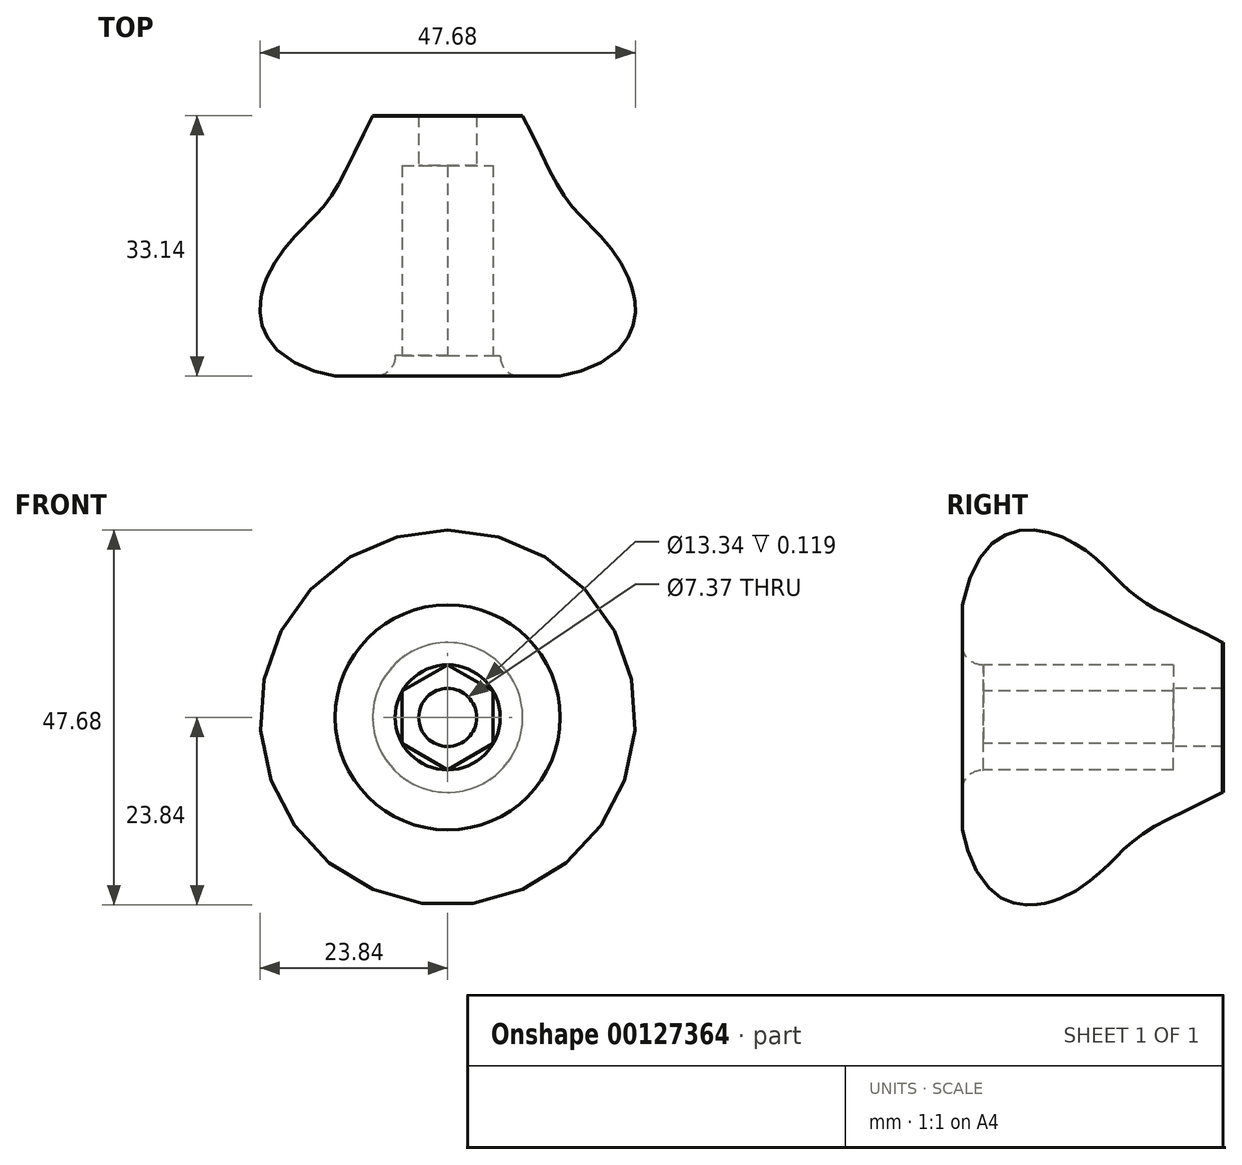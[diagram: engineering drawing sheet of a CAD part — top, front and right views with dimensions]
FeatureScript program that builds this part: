
annotation { "Feature Type Name" : "Feature", "Feature Type Description" : "" }
export const myFeature = defineFeature(function(context is Context, id is Id, definition is map)
    precondition{}
    {
        {
            var Q0;
            Q0=qCreatedBy(makeId("Front.planeOp"),FACE);
            var sketch = newSketch(context, id + "F0", { "sketchPlane" : qUnion([Q0])});
            skCircle(sketch, "E0", {"center": v(0, 0) * mm, "radius": 9.53 * mm});
            skSolve(sketch);
        }
        {
            var Q0;
            {var subQ0=sQuery(id+"F0.wireOp",EDGE,"E0");var subQ1=makeQuery(id+"F0.imprint","INTERSECT",VERTEX,{"derivedFrom":[subQ0,sQuery(id+"F0.wireOp",EDGE,"ea245839-a498-4638-985b-73fae0246c39")]});Q0=makeQuery(id+"F0.imprint","IMPRINT",FACE,{"disambiguationData":[TD([[makeQuery(id+"F0.imprint","IMPRINT",EDGE,{"disambiguationData":[TD([[subQ1,-1.0]])],"derivedFrom":subQ0}),1.0]])]});}
            var Q1;
            Q1=makeQuery(id+"F0.imprint","IMPRINT",FACE,{"disambiguationData":[TD([[makeQuery(id+"F0.imprint","IMPRINT",EDGE,{"derivedFrom":sQuery(id+"F0.wireOp",EDGE,"2dcc8b00-aa93-42b5-8a72-6d1d4eab4258")}),1.0]])]});
            extrude(context, id + "F1", {"entities" : qUnion([Q0, Q1]), "offsetDistance" : 25.4 * mm, "depth" : 15.24 * mm});
        }
        {
            var Q0;
            Q0=makeQuery(id+"F1.opExtrude","CAP_FACE",FACE,{"disambiguationData":[OSD([sQuery(id+"F0.wireOp",EDGE,"E0"),sQuery(id+"F0.wireOp",EDGE,"2dcc8b00-aa93-42b5-8a72-6d1d4eab4258"),sQuery(id+"F0.wireOp",EDGE,"ea245839-a498-4638-985b-73fae0246c39"),sQuery(id+"F0.wireOp",EDGE,"28ef0078-34b0-4df2-9f13-6cd2cfbab48c0.MirrorCS"),sQuery(id+"F0.wireOp",EDGE,"f54b358c-e5d3-4f08-8e52-d21b7307fad60.MirrorCS")])],"isStart":false});
            var sketch = newSketch(context, id + "F2", { "sketchPlane" : qUnion([Q0])});
            skCircle(sketch, "E1.cCircle", {"center": v(0, 0) * mm, "radius": 5.78 * mm, "construction": true});
            skLineSegment(sketch, "E1.0", {"start": v(5.78, 3.34) * mm, "end": v(5.78, -3.34) * mm});
            skLineSegment(sketch, "E1.1", {"start": v(5.78, -3.34) * mm, "end": v(0, -6.67) * mm});
            skLineSegment(sketch, "E1.2", {"start": v(0, -6.67) * mm, "end": v(-5.78, -3.34) * mm});
            skLineSegment(sketch, "E1.3", {"start": v(-5.78, -3.34) * mm, "end": v(-5.78, 3.34) * mm});
            skLineSegment(sketch, "E1.4", {"start": v(-5.78, 3.34) * mm, "end": v(0, 6.67) * mm});
            skLineSegment(sketch, "E1.5", {"start": v(0, 6.67) * mm, "end": v(5.78, 3.34) * mm});
            skPoint(sketch, "E1.0.midPoint", {"position": v(5.78, 0) * mm});
            skSolve(sketch);
        }
        {
            var Q0;
            Q0=makeQuery(id+"F2.imprint","IMPRINT",FACE,{"disambiguationData":[TD([[makeQuery(id+"F2.imprint","IMPRINT",EDGE,{"derivedFrom":sQuery(id+"F2.wireOp",EDGE,"E1.0")}),-1.0]])]});
            extrude(context, id + "F3", {"entities" : qUnion([Q0]), "operationType" : NewBodyOperationType.REMOVE, "oppositeDirection" : true, "depth" : 8.9 * mm});
        }
        {
            var Q0;
            Q0=makeQuery(id+"F3.boolean.opBoolean","COPY",FACE,{"derivedFrom":makeQuery(id+"F3.opExtrude","CAP_FACE",FACE,{"disambiguationData":[OSD([sQuery(id+"F2.wireOp",EDGE,"E1.0"),sQuery(id+"F2.wireOp",EDGE,"E1.1"),sQuery(id+"F2.wireOp",EDGE,"E1.2"),sQuery(id+"F2.wireOp",EDGE,"E1.3"),sQuery(id+"F2.wireOp",EDGE,"E1.4"),sQuery(id+"F2.wireOp",EDGE,"E1.5")])],"isStart":false})});
            var sketch = newSketch(context, id + "F4", { "sketchPlane" : qUnion([Q0])});
            skCircle(sketch, "E2", {"center": v(0, 0) * mm, "radius": 3.68 * mm});
            skSolve(sketch);
        }
        {
            var Q0;
            Q0=makeQuery(id+"F4.imprint","IMPRINT",FACE,{"disambiguationData":[TD([[makeQuery(id+"F4.imprint","IMPRINT",EDGE,{"derivedFrom":sQuery(id+"F4.wireOp",EDGE,"E2")}),1.0]])]});
            extrude(context, id + "F5", {"entities" : qUnion([Q0]), "operationType" : NewBodyOperationType.REMOVE, "endBound" : BoundingType.THROUGH_ALL, "oppositeDirection" : true, "offsetDistance" : 25.4 * mm, "depth" : 25.4 * mm});
        }
        {
            var Q0;
            Q0=qCreatedBy(makeId("Right.planeOp"),FACE);
            var sketch = newSketch(context, id + "F6", { "sketchPlane" : qUnion([Q0])});
            skLineSegment(sketch, "E3", {"start": v(-33.14, -14.3) * mm, "end": v(-33.14, -14.3) * mm});
            skLineSegment(sketch, "E4", {"start": v(-33.14, -14.3) * mm, "end": v(-33.14, 3.71) * mm});
            skLineSegment(sketch, "E5", {"start": v(0, -6.67) * mm, "end": v(-33.14, -6.67) * mm});
            skLineSegment(sketch, "E6", {"start": v(-33.14, 3.71) * mm, "end": v(-33.14, -6.67) * mm});
            skLineSegment(sketch, "E7", {"start": v(0, -6.67) * mm, "end": v(0, -9.47) * mm});
            skFitSpline(sketch, "E8", {"points": [v(0, -9.47) * mm, v(-11.54, -15.77) * mm, v(-19.8, -22.6) * mm, v(-33.14, -14.3) * mm], "startDerivative": vector(-54.08, -28.43) * mm, "endDerivative": vector(-17.97, 89.59) * mm});
            skLineSegment(sketch, "E9", {"start": v(0, 0) * mm, "end": v(-22.32, 0) * mm});
            skSolve(sketch);
        }
        {
            var Q0;
            Q0=makeQuery(id+"F6.imprint","IMPRINT",FACE,{"disambiguationData":[TD([[makeQuery(id+"F6.imprint","IMPRINT",EDGE,{"derivedFrom":sQuery(id+"F6.wireOp",EDGE,"E3")}),-1.0]])]});
            var Q1;
            Q1=makeQuery(id+"F6.imprint","IMPRINT",FACE,{"disambiguationData":[TD([[makeQuery(id+"F6.imprint","IMPRINT",EDGE,{"derivedFrom":sQuery(id+"F6.wireOp",EDGE,"E4")}),-1.0]])]});
            var Q2;
            Q2=sQuery(id+"F6.wireOp",EDGE,"E9");
            revolve(context, id + "F7", {"operationType" : NewBodyOperationType.ADD, "surfaceOperationType" : NewSurfaceOperationType.NEW, "entities" : qUnion([Q0, Q1]), "axis" : qUnion([Q2]), "revolveType" : RevolveType.FULL});
        }
        {
            var Q0;
            Q0=makeQuery(id+"F7.opRevolve","SWEPT_EDGE",EDGE,{"disambiguationData":[OSD([sQuery(id+"F6.wireOp",EDGE,"E5"),sQuery(id+"F6.wireOp",EDGE,"E6")])]});
            fillet(context, id + "F8", {"entities" : qUnion([Q0]), "radius" : 2.54 * mm, "tangentPropagation" : true, "allowEdgeOverflow" : false});
        }
        {
            var Q0;
            {var subQ0=makeQuery(id+"F1.opExtrude","CAP_FACE",FACE,{"disambiguationData":[OSD([sQuery(id+"F0.wireOp",EDGE,"E0")])],"isStart":false});Q0=makeQuery(id+"F7.boolean.opBoolean","SPLIT",FACE,{"disambiguationData":[TD([subQ0,makeQuery(id+"F3.boolean.opBoolean","COPY",FACE,{"derivedFrom":makeQuery(id+"F3.opExtrude","SWEPT_FACE",FACE,{"disambiguationData":[OSD([sQuery(id+"F2.wireOp",EDGE,"E1.3")])]})}),makeQuery(id+"F3.boolean.opBoolean","COPY",FACE,{"derivedFrom":makeQuery(id+"F3.opExtrude","SWEPT_FACE",FACE,{"disambiguationData":[OSD([sQuery(id+"F2.wireOp",EDGE,"E1.4")])]})}),makeQuery(id+"F3.boolean.opBoolean","COPY",FACE,{"derivedFrom":makeQuery(id+"F3.opExtrude","SWEPT_FACE",FACE,{"disambiguationData":[OSD([sQuery(id+"F2.wireOp",EDGE,"E1.5")])]})}),makeQuery(id+"F7.opRevolve","SWEPT_FACE",FACE,{"disambiguationData":[OSD([sQuery(id+"F6.wireOp",EDGE,"E5")])]})])],"derivedFrom":subQ0});}
            var Q1;
            {var subQ0=makeQuery(id+"F1.opExtrude","CAP_FACE",FACE,{"disambiguationData":[OSD([sQuery(id+"F0.wireOp",EDGE,"E0")])],"isStart":false});Q1=makeQuery(id+"F7.boolean.opBoolean","SPLIT",FACE,{"disambiguationData":[TD([subQ0,makeQuery(id+"F3.boolean.opBoolean","COPY",FACE,{"derivedFrom":makeQuery(id+"F3.opExtrude","SWEPT_FACE",FACE,{"disambiguationData":[OSD([sQuery(id+"F2.wireOp",EDGE,"E1.2")])]})}),makeQuery(id+"F3.boolean.opBoolean","COPY",FACE,{"derivedFrom":makeQuery(id+"F3.opExtrude","SWEPT_FACE",FACE,{"disambiguationData":[OSD([sQuery(id+"F2.wireOp",EDGE,"E1.3")])]})}),makeQuery(id+"F3.boolean.opBoolean","COPY",FACE,{"derivedFrom":makeQuery(id+"F3.opExtrude","SWEPT_FACE",FACE,{"disambiguationData":[OSD([sQuery(id+"F2.wireOp",EDGE,"E1.4")])]})}),makeQuery(id+"F7.opRevolve","SWEPT_FACE",FACE,{"disambiguationData":[OSD([sQuery(id+"F6.wireOp",EDGE,"E5")])]})])],"derivedFrom":subQ0});}
            var Q2;
            {var subQ0=makeQuery(id+"F1.opExtrude","CAP_FACE",FACE,{"disambiguationData":[OSD([sQuery(id+"F0.wireOp",EDGE,"E0")])],"isStart":false});Q2=makeQuery(id+"F7.boolean.opBoolean","SPLIT",FACE,{"disambiguationData":[TD([subQ0,makeQuery(id+"F3.boolean.opBoolean","COPY",FACE,{"derivedFrom":makeQuery(id+"F3.opExtrude","SWEPT_FACE",FACE,{"disambiguationData":[OSD([sQuery(id+"F2.wireOp",EDGE,"E1.1")])]})}),makeQuery(id+"F3.boolean.opBoolean","COPY",FACE,{"derivedFrom":makeQuery(id+"F3.opExtrude","SWEPT_FACE",FACE,{"disambiguationData":[OSD([sQuery(id+"F2.wireOp",EDGE,"E1.2")])]})}),makeQuery(id+"F3.boolean.opBoolean","COPY",FACE,{"derivedFrom":makeQuery(id+"F3.opExtrude","SWEPT_FACE",FACE,{"disambiguationData":[OSD([sQuery(id+"F2.wireOp",EDGE,"E1.3")])]})}),makeQuery(id+"F7.opRevolve","SWEPT_FACE",FACE,{"disambiguationData":[OSD([sQuery(id+"F6.wireOp",EDGE,"E5")])]})])],"derivedFrom":subQ0});}
            var Q3;
            {var subQ0=makeQuery(id+"F1.opExtrude","CAP_FACE",FACE,{"disambiguationData":[OSD([sQuery(id+"F0.wireOp",EDGE,"E0")])],"isStart":false});Q3=makeQuery(id+"F7.boolean.opBoolean","SPLIT",FACE,{"disambiguationData":[TD([subQ0,makeQuery(id+"F3.boolean.opBoolean","COPY",FACE,{"derivedFrom":makeQuery(id+"F3.opExtrude","SWEPT_FACE",FACE,{"disambiguationData":[OSD([sQuery(id+"F2.wireOp",EDGE,"E1.0")])]})}),makeQuery(id+"F3.boolean.opBoolean","COPY",FACE,{"derivedFrom":makeQuery(id+"F3.opExtrude","SWEPT_FACE",FACE,{"disambiguationData":[OSD([sQuery(id+"F2.wireOp",EDGE,"E1.1")])]})}),makeQuery(id+"F3.boolean.opBoolean","COPY",FACE,{"derivedFrom":makeQuery(id+"F3.opExtrude","SWEPT_FACE",FACE,{"disambiguationData":[OSD([sQuery(id+"F2.wireOp",EDGE,"E1.5")])]})}),makeQuery(id+"F7.opRevolve","SWEPT_FACE",FACE,{"disambiguationData":[OSD([sQuery(id+"F6.wireOp",EDGE,"E5")])]})])],"derivedFrom":subQ0});}
            var Q4;
            {var subQ0=makeQuery(id+"F1.opExtrude","CAP_FACE",FACE,{"disambiguationData":[OSD([sQuery(id+"F0.wireOp",EDGE,"E0")])],"isStart":false});Q4=makeQuery(id+"F7.boolean.opBoolean","SPLIT",FACE,{"disambiguationData":[TD([subQ0,makeQuery(id+"F3.boolean.opBoolean","COPY",FACE,{"derivedFrom":makeQuery(id+"F3.opExtrude","SWEPT_FACE",FACE,{"disambiguationData":[OSD([sQuery(id+"F2.wireOp",EDGE,"E1.0")])]})}),makeQuery(id+"F3.boolean.opBoolean","COPY",FACE,{"derivedFrom":makeQuery(id+"F3.opExtrude","SWEPT_FACE",FACE,{"disambiguationData":[OSD([sQuery(id+"F2.wireOp",EDGE,"E1.1")])]})}),makeQuery(id+"F3.boolean.opBoolean","COPY",FACE,{"derivedFrom":makeQuery(id+"F3.opExtrude","SWEPT_FACE",FACE,{"disambiguationData":[OSD([sQuery(id+"F2.wireOp",EDGE,"E1.2")])]})}),makeQuery(id+"F7.opRevolve","SWEPT_FACE",FACE,{"disambiguationData":[OSD([sQuery(id+"F6.wireOp",EDGE,"E5")])]})])],"derivedFrom":subQ0});}
            var Q5;
            {var subQ0=makeQuery(id+"F1.opExtrude","CAP_FACE",FACE,{"disambiguationData":[OSD([sQuery(id+"F0.wireOp",EDGE,"E0")])],"isStart":false});Q5=makeQuery(id+"F7.boolean.opBoolean","SPLIT",FACE,{"disambiguationData":[TD([subQ0,makeQuery(id+"F3.boolean.opBoolean","COPY",FACE,{"derivedFrom":makeQuery(id+"F3.opExtrude","SWEPT_FACE",FACE,{"disambiguationData":[OSD([sQuery(id+"F2.wireOp",EDGE,"E1.0")])]})}),makeQuery(id+"F3.boolean.opBoolean","COPY",FACE,{"derivedFrom":makeQuery(id+"F3.opExtrude","SWEPT_FACE",FACE,{"disambiguationData":[OSD([sQuery(id+"F2.wireOp",EDGE,"E1.4")])]})}),makeQuery(id+"F3.boolean.opBoolean","COPY",FACE,{"derivedFrom":makeQuery(id+"F3.opExtrude","SWEPT_FACE",FACE,{"disambiguationData":[OSD([sQuery(id+"F2.wireOp",EDGE,"E1.5")])]})}),makeQuery(id+"F7.opRevolve","SWEPT_FACE",FACE,{"disambiguationData":[OSD([sQuery(id+"F6.wireOp",EDGE,"E5")])]})])],"derivedFrom":subQ0});}
            extrude(context, id + "F9", {"entities" : qUnion([Q0, Q1, Q2, Q3, Q4, Q5]), "operationType" : NewBodyOperationType.ADD, "depth" : 15.24 * mm, "offsetDistance" : 25.4 * mm});
        }
    });
